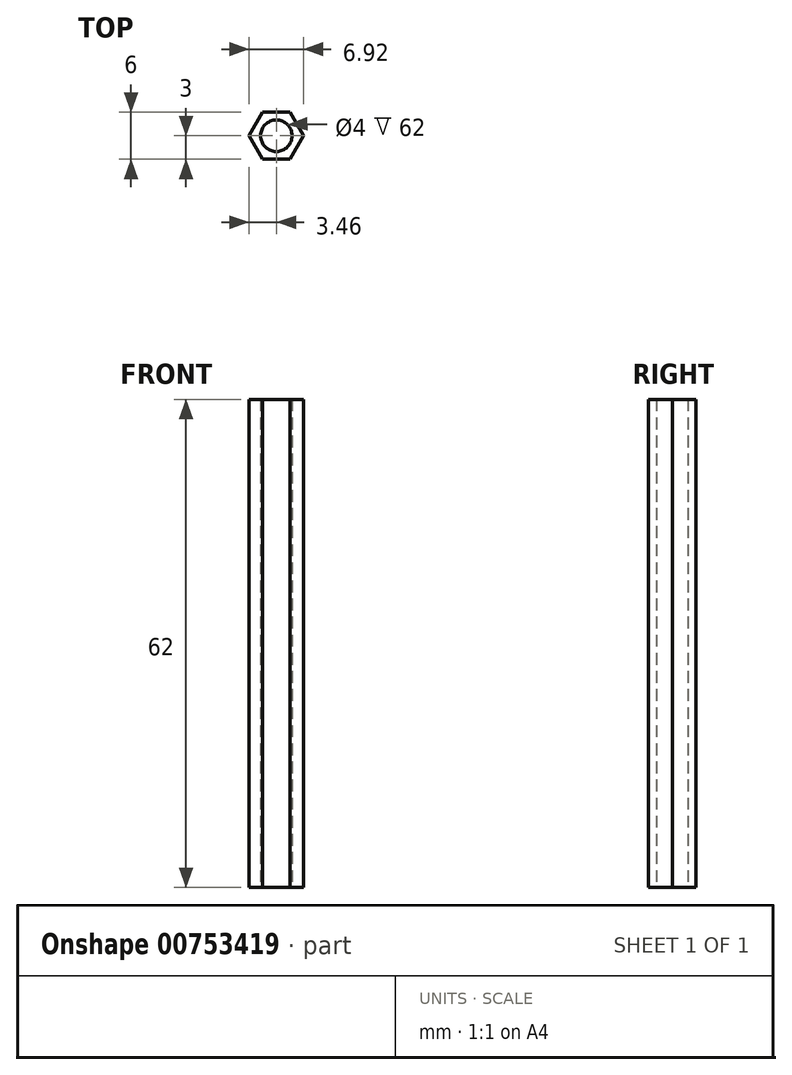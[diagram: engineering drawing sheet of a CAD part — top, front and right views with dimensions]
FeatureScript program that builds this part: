
annotation { "Feature Type Name" : "Feature", "Feature Type Description" : "" }
export const myFeature = defineFeature(function(context is Context, id is Id, definition is map)
    precondition{}
    {
        {
            var Q0;
            Q0=qCreatedBy(makeId("Top.planeOp"),FACE);
            var sketch = newSketch(context, id + "F0", { "sketchPlane" : qUnion([Q0])});
            skCircle(sketch, "E0", {"center": v(0, 0) * mm, "radius": 2 * mm});
            skCircle(sketch, "E1", {"center": v(0, 0) * mm, "radius": 3 * mm});
            skCircle(sketch, "E2.cCircle", {"center": v(0, 0) * mm, "radius": 3 * mm, "construction": true});
            skLineSegment(sketch, "E2.0", {"start": v(-1.73, 3) * mm, "end": v(1.73, 3) * mm});
            skLineSegment(sketch, "E2.1", {"start": v(1.73, 3) * mm, "end": v(3.46, 0) * mm});
            skLineSegment(sketch, "E2.2", {"start": v(3.46, 0) * mm, "end": v(1.73, -3) * mm});
            skLineSegment(sketch, "E2.3", {"start": v(1.73, -3) * mm, "end": v(-1.73, -3) * mm});
            skLineSegment(sketch, "E2.4", {"start": v(-1.73, -3) * mm, "end": v(-3.46, 0) * mm});
            skLineSegment(sketch, "E2.5", {"start": v(-3.46, 0) * mm, "end": v(-1.73, 3) * mm});
            skPoint(sketch, "E2.0.midPoint", {"position": v(0, 3) * mm});
            skSolve(sketch);
        }
        {
            var Q0;
            Q0 = qSketchRegion(id + "F0", true);
            extrude(context, id + "F1", {"entities" : qUnion([Q0]), "depth" : 62 * mm, "offsetDistance" : 25 * mm});
        }
    });
